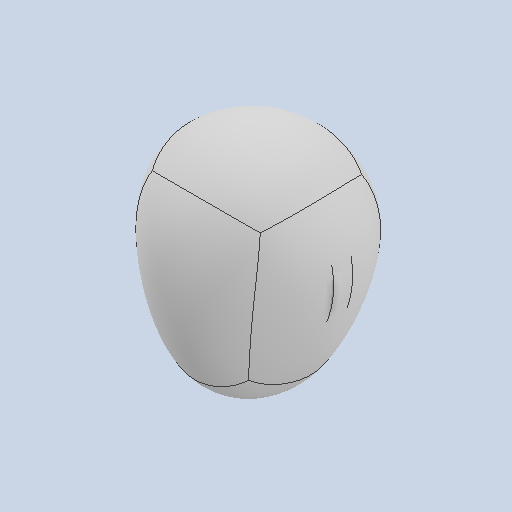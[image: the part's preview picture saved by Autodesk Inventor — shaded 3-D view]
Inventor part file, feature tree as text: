
AUTODESK INVENTOR PART (.ipt)
format: ipt  version: 2024.2 (Build 282272000, 272)  size: 317,952 bytes
history: native  units: mm
features: other x2, extrude x2, sketch x1
ambient origin geometry x8: Origin, YZ Plane, XZ Plane, XY Plane, X Axis, Y Axis, Z Axis, Center Point
bodies: Solid3 (feature_tree)
feature tree (5):
  other  "Твердое тело1"
  extrude  "Выдавливание1"  Depth=180.0mm
  other  "Form2"
  extrude  "Extrusion2"  Depth=120.0mm
  sketch  "Эскиз1"
